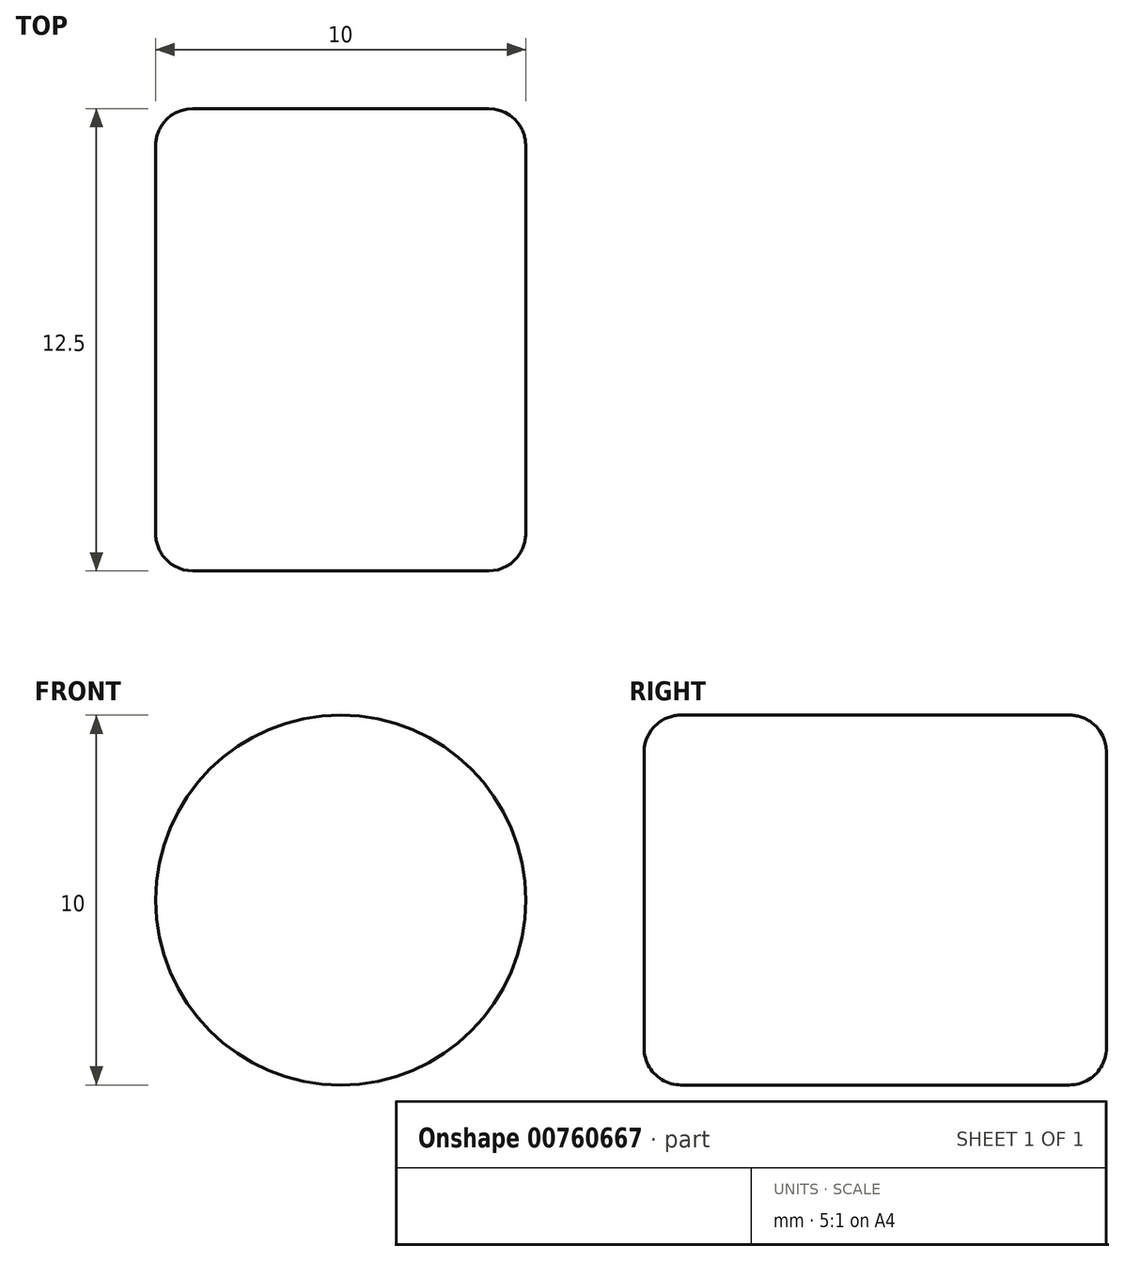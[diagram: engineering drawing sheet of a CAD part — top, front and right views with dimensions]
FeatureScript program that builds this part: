
annotation { "Feature Type Name" : "Feature", "Feature Type Description" : "" }
export const myFeature = defineFeature(function(context is Context, id is Id, definition is map)
    precondition{}
    {
        {
            var Q0;
            Q0=qCreatedBy(makeId("Front.planeOp"),FACE);
            var sketch = newSketch(context, id + "F0", { "sketchPlane" : qUnion([Q0])});
            skCircle(sketch, "E0", {"center": v(0, 0) * mm, "radius": 5 * mm});
            skSolve(sketch);
        }
        {
            var Q0;
            Q0 = qSketchRegion(id + "F0", true);
            extrude(context, id + "F1", {"entities" : qUnion([Q0]), "depth" : 12.5 * mm, "offsetDistance" : 25 * mm});
        }
        {
            var Q0;
            Q0=makeQuery(id+"F1.opExtrude","CAP_FACE",FACE,{"disambiguationData":[OSD([sQuery(id+"F0.wireOp",EDGE,"E0")])],"isStart":false});
            var Q1;
            Q1=makeQuery(id+"F1.opExtrude","CAP_EDGE",EDGE,{"disambiguationData":[OSD([sQuery(id+"F0.wireOp",EDGE,"E0")])],"isStart":true});
            fillet(context, id + "F2", {"entities" : qUnion([Q0, Q1]), "radius" : 1 * mm, "tangentPropagation" : true, "allowEdgeOverflow" : false});
        }
    });
